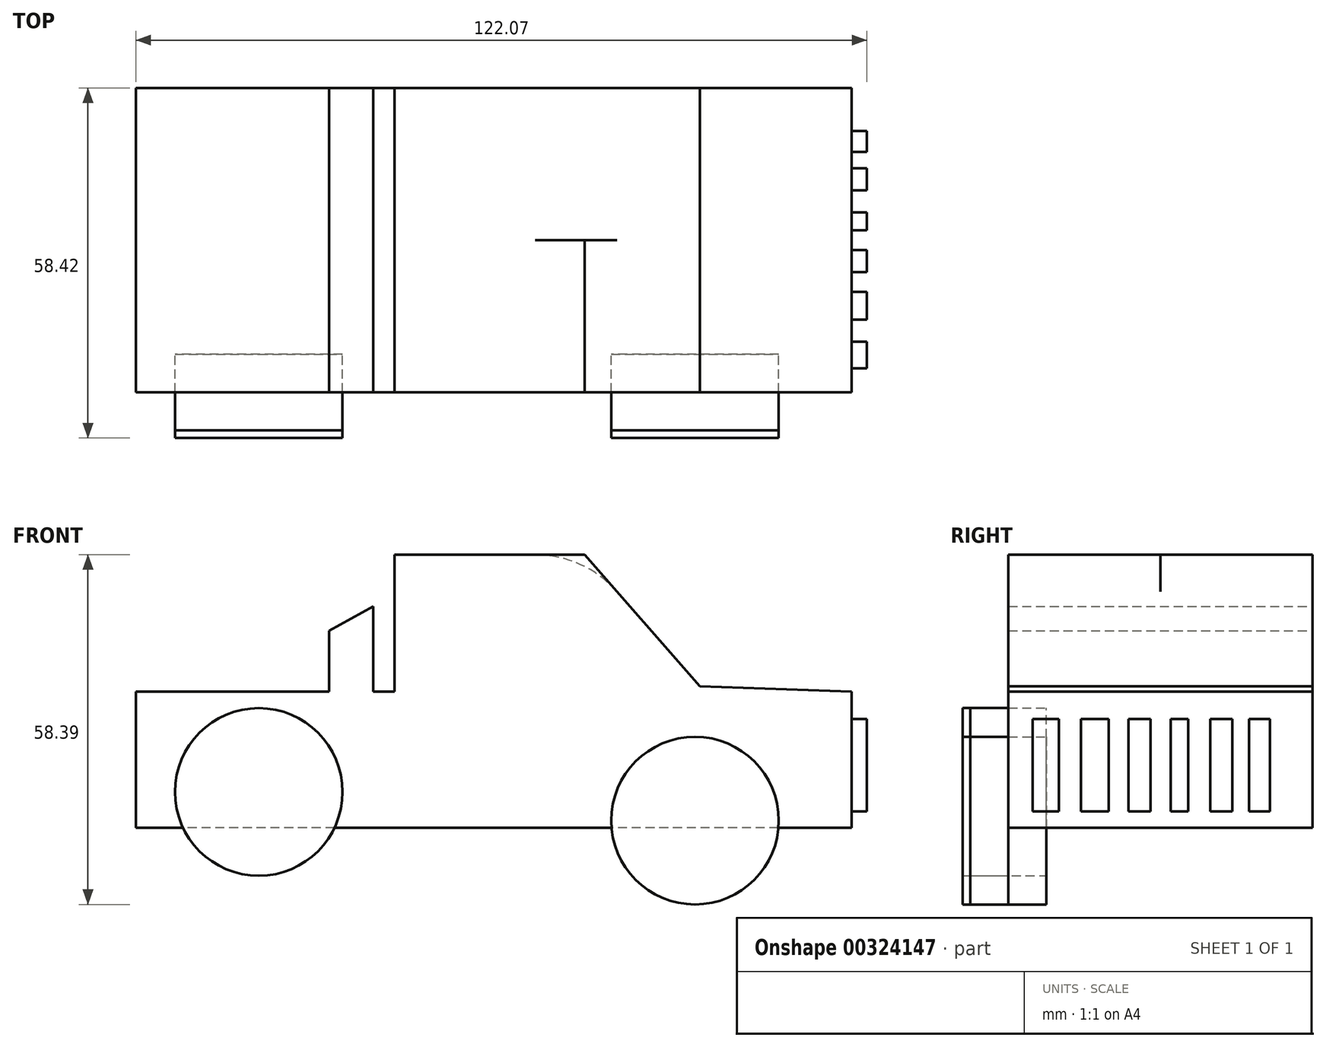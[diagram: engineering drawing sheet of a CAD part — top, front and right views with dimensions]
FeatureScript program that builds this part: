
annotation { "Feature Type Name" : "Feature", "Feature Type Description" : "" }
export const myFeature = defineFeature(function(context is Context, id is Id, definition is map)
    precondition{}
    {
        {
            var Q0;
            Q0=qCreatedBy(makeId("Front.planeOp"),FACE);
            var sketch = newSketch(context, id + "F0", { "sketchPlane" : qUnion([Q0])});
            skLineSegment(sketch, "E0", {"start": v(-43.82, 6.7) * mm, "end": v(-61.53, 6.7) * mm});
            skLineSegment(sketch, "E1", {"start": v(-61.53, 6.7) * mm, "end": v(-61.53, 29.43) * mm});
            skLineSegment(sketch, "E2", {"start": v(-61.53, 29.43) * mm, "end": v(-18.36, 29.43) * mm});
            skLineSegment(sketch, "E3", {"start": v(-18.36, 29.43) * mm, "end": v(-18.36, 52.3) * mm});
            skLineSegment(sketch, "E4", {"start": v(-18.36, 52.3) * mm, "end": v(13.39, 52.3) * mm});
            skLineSegment(sketch, "E5", {"start": v(13.39, 52.3) * mm, "end": v(32.61, 30.3) * mm});
            skLineSegment(sketch, "E6", {"start": v(32.61, 30.3) * mm, "end": v(58, 29.43) * mm});
            skLineSegment(sketch, "E7", {"start": v(22.23, 6.7) * mm, "end": v(-22.23, 6.7) * mm});
            skLineSegment(sketch, "E8", {"start": v(43.82, 6.7) * mm, "end": v(58, 6.7) * mm});
            skLineSegment(sketch, "E9", {"start": v(58, 29.43) * mm, "end": v(58, 6.7) * mm});
            skLineSegment(sketch, "E10", {"start": v(-29.3, 29.43) * mm, "end": v(-29.3, 39.59) * mm});
            skLineSegment(sketch, "E11", {"start": v(-29.3, 39.59) * mm, "end": v(-21.9, 43.65) * mm});
            skLineSegment(sketch, "E12", {"start": v(-21.9, 43.65) * mm, "end": v(-21.9, 29.43) * mm});
            skLineSegment(sketch, "E13", {"start": v(-61.53, 15.6) * mm, "end": v(-54.97, 15.6) * mm});
            skLineSegment(sketch, "E14", {"start": v(-54.97, 15.6) * mm, "end": v(-54.97, 6.7) * mm});
            skLineSegment(sketch, "E15", {"start": v(58, 21.75) * mm, "end": v(51.6, 21.75) * mm});
            skLineSegment(sketch, "E16", {"start": v(51.6, 21.75) * mm, "end": v(51.6, 29.43) * mm});
            skLineSegment(sketch, "E17", {"start": v(-54.97, 6.7) * mm, "end": v(58, 6.7) * mm});
            skSolve(sketch);
        }
        {
            var Q0;
            Q0 = qSketchRegion(id + "F0", true);
            extrude(context, id + "F1", {"entities" : qUnion([Q0]), "depth" : 50.8 * mm, "symmetric" : true});
        }
        {
            var Q0;
            Q0=makeQuery(id+"F1.opExtrude","CAP_FACE",FACE,{"disambiguationData":[OSD([sQuery(id+"F0.wireOp",EDGE,"jsAS9IXH-zQaz-s3Kv-pUAx-luXk4qnFeEN5"),sQuery(id+"F0.wireOp",EDGE,"7l7WPdtS-5suQ-AHQC-gmTl-FT6wHJ7VEzlQ"),sQuery(id+"F0.wireOp",EDGE,"E0"),sQuery(id+"F0.wireOp",EDGE,"E1"),sQuery(id+"F0.wireOp",EDGE,"E2"),sQuery(id+"F0.wireOp",EDGE,"E3"),sQuery(id+"F0.wireOp",EDGE,"E4"),sQuery(id+"F0.wireOp",EDGE,"E5"),sQuery(id+"F0.wireOp",EDGE,"E6"),sQuery(id+"F0.wireOp",EDGE,"E7"),sQuery(id+"F0.wireOp",EDGE,"qzmlPklc-gSGK-qsKq-jCsS-Svxx3mp7mvPV"),sQuery(id+"F0.wireOp",EDGE,"ulWVZydW-LgJQ-jYxT-eYgx-awK6DR7PkJde"),sQuery(id+"F0.wireOp",EDGE,"E8"),sQuery(id+"F0.wireOp",EDGE,"E9"),sQuery(id+"F0.wireOp",EDGE,"E10"),sQuery(id+"F0.wireOp",EDGE,"E11"),sQuery(id+"F0.wireOp",EDGE,"E12")])],"isStart":false});
            var sketch = newSketch(context, id + "F2", { "sketchPlane" : qUnion([Q0])});
            skLineSegment(sketch, "E18", {"start": v(-14.85, 49.04) * mm, "end": v(-14.85, 30.46) * mm});
            skLineSegment(sketch, "E19", {"start": v(-14.85, 30.46) * mm, "end": v(27.46, 30.46) * mm});
            skLineSegment(sketch, "E20", {"start": v(27.46, 30.46) * mm, "end": v(12.86, 49.04) * mm});
            skLineSegment(sketch, "E21", {"start": v(12.86, 49.04) * mm, "end": v(-14.85, 49.04) * mm});
            skSolve(sketch);
        }
        {
            var Q0;
            Q0=makeQuery(id+"F2.imprint","IMPRINT",FACE,{"disambiguationData":[TD([[makeQuery(id+"F2.imprint","IMPRINT",EDGE,{"derivedFrom":sQuery(id+"F2.wireOp",EDGE,"E18")}),1.0]])]});
            extrude(context, id + "F3", {"entities" : qUnion([Q0]), "operationType" : NewBodyOperationType.REMOVE, "oppositeDirection" : true, "depth" : 6.35 * mm});
        }
        {
            var Q0;
            Q0=makeQuery(id+"F1.opExtrude","SWEPT_EDGE",EDGE,{"disambiguationData":[OSD([sQuery(id+"F0.wireOp",EDGE,"E4"),sQuery(id+"F0.wireOp",EDGE,"E5")])]});
            fillet(context, id + "F4", {"entities" : qUnion([Q0]), "radius" : 18.1 * mm, "tangentPropagation" : true, "allowEdgeOverflow" : false});
        }
        {
            var Q0;
            Q0=makeQuery(id+"F1.opExtrude","SWEPT_FACE",FACE,{"disambiguationData":[OSD([sQuery(id+"F0.wireOp",EDGE,"E9")])]});
            var sketch = newSketch(context, id + "F5", { "sketchPlane" : qUnion([Q0])});
            skLineSegment(sketch, "E22.bottom", {"start": v(-21.39, 24.89) * mm, "end": v(21.75, 24.89) * mm});
            skLineSegment(sketch, "E22.top", {"start": v(-21.39, 9.4) * mm, "end": v(21.75, 9.4) * mm});
            skLineSegment(sketch, "E22.left", {"start": v(-21.39, 24.89) * mm, "end": v(-21.39, 9.4) * mm});
            skLineSegment(sketch, "E22.right", {"start": v(21.75, 24.89) * mm, "end": v(21.75, 9.4) * mm});
            skLineSegment(sketch, "E23", {"start": v(-16.96, 24.89) * mm, "end": v(-16.96, 9.4) * mm});
            skLineSegment(sketch, "E24", {"start": v(-13.27, 24.89) * mm, "end": v(-13.27, 9.4) * mm});
            skLineSegment(sketch, "E25", {"start": v(-8.66, 24.89) * mm, "end": v(-8.66, 9.4) * mm});
            skLineSegment(sketch, "E26", {"start": v(-5.35, 24.89) * mm, "end": v(-5.35, 9.4) * mm});
            skLineSegment(sketch, "E27", {"start": v(-1.66, 24.89) * mm, "end": v(-1.66, 9.4) * mm});
            skLineSegment(sketch, "E28", {"start": v(1.66, 24.89) * mm, "end": v(1.66, 9.4) * mm});
            skLineSegment(sketch, "E29", {"start": v(4.6, 24.89) * mm, "end": v(4.6, 9.4) * mm});
            skLineSegment(sketch, "E30", {"start": v(8.3, 24.89) * mm, "end": v(8.3, 9.4) * mm});
            skLineSegment(sketch, "E31", {"start": v(11.98, 24.89) * mm, "end": v(11.98, 9.4) * mm});
            skLineSegment(sketch, "E32", {"start": v(14.75, 24.89) * mm, "end": v(14.75, 9.4) * mm});
            skLineSegment(sketch, "E33", {"start": v(18.25, 24.89) * mm, "end": v(18.25, 9.4) * mm});
            skSolve(sketch);
        }
        {
            var Q0;
            {var subQ0=sQuery(id+"F5.wireOp",EDGE,"E22.left");Q0=makeQuery(id+"F5.imprint","IMPRINT",FACE,{"disambiguationData":[TD([[makeQuery(id+"F5.imprint","IMPRINT",EDGE,{"derivedFrom":subQ0}),1.0]])]});}
            var Q1;
            {var subQ0=sQuery(id+"F5.wireOp",EDGE,"E24");Q1=makeQuery(id+"F5.imprint","IMPRINT",FACE,{"disambiguationData":[TD([[makeQuery(id+"F5.imprint","IMPRINT",EDGE,{"derivedFrom":subQ0}),1.0]])]});}
            var Q2;
            {var subQ0=sQuery(id+"F5.wireOp",EDGE,"E26");Q2=makeQuery(id+"F5.imprint","IMPRINT",FACE,{"disambiguationData":[TD([[makeQuery(id+"F5.imprint","IMPRINT",EDGE,{"derivedFrom":subQ0}),1.0]])]});}
            var Q3;
            {var subQ0=sQuery(id+"F5.wireOp",EDGE,"E28");Q3=makeQuery(id+"F5.imprint","IMPRINT",FACE,{"disambiguationData":[TD([[makeQuery(id+"F5.imprint","IMPRINT",EDGE,{"derivedFrom":subQ0}),1.0]])]});}
            var Q4;
            {var subQ0=sQuery(id+"F5.wireOp",EDGE,"E30");Q4=makeQuery(id+"F5.imprint","IMPRINT",FACE,{"disambiguationData":[TD([[makeQuery(id+"F5.imprint","IMPRINT",EDGE,{"derivedFrom":subQ0}),1.0]])]});}
            var Q5;
            {var subQ0=sQuery(id+"F5.wireOp",EDGE,"E32");Q5=makeQuery(id+"F5.imprint","IMPRINT",FACE,{"disambiguationData":[TD([[makeQuery(id+"F5.imprint","IMPRINT",EDGE,{"derivedFrom":subQ0}),1.0]])]});}
            extrude(context, id + "F6", {"entities" : qUnion([Q0, Q1, Q2, Q3, Q4, Q5]), "operationType" : NewBodyOperationType.ADD, "depth" : 2.54 * mm});
        }
        {
            var Q0;
            Q0 = qSketchRegion(id + "F0", true);
            extrude(context, id + "F7", {"entities" : qUnion([Q0]), "operationType" : NewBodyOperationType.ADD, "depth" : 25.4 * mm});
        }
        {
            var Q0;
            {var subQ0=sQuery(id+"F0.wireOp",EDGE,"E17");var subQ1=sQuery(id+"F0.wireOp",EDGE,"E12");var subQ2=sQuery(id+"F0.wireOp",EDGE,"E11");var subQ3=sQuery(id+"F0.wireOp",EDGE,"E10");var subQ4=sQuery(id+"F0.wireOp",EDGE,"E9");var subQ5=sQuery(id+"F0.wireOp",EDGE,"E6");var subQ6=sQuery(id+"F0.wireOp",EDGE,"E5");var subQ7=sQuery(id+"F0.wireOp",EDGE,"E4");var subQ8=sQuery(id+"F0.wireOp",EDGE,"E3");var subQ9=sQuery(id+"F0.wireOp",EDGE,"E2");var subQ10=sQuery(id+"F0.wireOp",EDGE,"E1");var subQ11=sQuery(id+"F0.wireOp",EDGE,"E0");Q0=makeQuery(id+"F7.boolean.opBoolean","MERGE",FACE,{"derivedFrom":[makeQuery(id+"F1.opExtrude","CAP_FACE",FACE,{"disambiguationData":[OSD([subQ11,subQ10,subQ9,subQ8,subQ7,subQ6,subQ5,subQ4,subQ3,subQ2,subQ1,subQ0])],"isStart":false}),makeQuery(id+"F7.opExtrude","CAP_FACE",FACE,{"disambiguationData":[OSD([subQ11,subQ10,subQ9,subQ8,subQ7,subQ6,subQ5,subQ4,subQ3,subQ2,subQ1,subQ0])],"isStart":false})]});}
            var sketch = newSketch(context, id + "F8", { "sketchPlane" : qUnion([Q0])});
            skArc(sketch, "E34", {"start": v(-53.66, 6.7) * mm, "mid": v(-41.02, -1.3) * mm, "end": v(-28.38, 6.7) * mm});
            skArc(sketch, "E35", {"start": v(17.88, 6.7) * mm, "mid": v(31.82, -6.1) * mm, "end": v(45.76, 6.7) * mm});
            skArc(sketch, "E36", {"start": v(-28.38, 6.7) * mm, "mid": v(-41.02, 26.67) * mm, "end": v(-53.66, 6.7) * mm});
            skArc(sketch, "E37", {"start": v(45.76, 6.7) * mm, "mid": v(31.82, 21.88) * mm, "end": v(17.88, 6.7) * mm});
            skSolve(sketch);
        }
        {
            var Q0;
            {var subQ0=sQuery(id+"F8.wireOp",EDGE,"E34");Q0=makeQuery(id+"F8.imprint","IMPRINT",FACE,{"disambiguationData":[TD([[makeQuery(id+"F8.imprint","IMPRINT",EDGE,{"derivedFrom":subQ0}),1.0]])]});}
            var Q1;
            {var subQ0=sQuery(id+"F8.wireOp",EDGE,"E36");Q1=makeQuery(id+"F8.imprint","IMPRINT",FACE,{"disambiguationData":[TD([[makeQuery(id+"F8.imprint","IMPRINT",EDGE,{"derivedFrom":subQ0}),1.0]])]});}
            var Q2;
            {var subQ0=sQuery(id+"F8.wireOp",EDGE,"E37");Q2=makeQuery(id+"F8.imprint","IMPRINT",FACE,{"disambiguationData":[TD([[makeQuery(id+"F8.imprint","IMPRINT",EDGE,{"derivedFrom":subQ0}),1.0]])]});}
            var Q3;
            {var subQ0=sQuery(id+"F8.wireOp",EDGE,"E34");Q3=makeQuery(id+"F8.imprint","IMPRINT",FACE,{"disambiguationData":[TD([[makeQuery(id+"F8.imprint","IMPRINT",EDGE,{"derivedFrom":subQ0}),1.0]])]});}
            var Q4;
            {var subQ0=sQuery(id+"F8.wireOp",EDGE,"E35");Q4=makeQuery(id+"F8.imprint","IMPRINT",FACE,{"disambiguationData":[TD([[makeQuery(id+"F8.imprint","IMPRINT",EDGE,{"derivedFrom":subQ0}),1.0]])]});}
            var Q5;
            {var subQ0=sQuery(id+"F8.wireOp",EDGE,"E36");Q5=makeQuery(id+"F8.imprint","IMPRINT",FACE,{"disambiguationData":[TD([[makeQuery(id+"F8.imprint","IMPRINT",EDGE,{"derivedFrom":subQ0}),1.0]])]});}
            var Q6;
            {var subQ0=sQuery(id+"F8.wireOp",EDGE,"E37");Q6=makeQuery(id+"F8.imprint","IMPRINT",FACE,{"disambiguationData":[TD([[makeQuery(id+"F8.imprint","IMPRINT",EDGE,{"derivedFrom":subQ0}),1.0]])]});}
            var Q7;
            {var subQ0=sQuery(id+"F8.wireOp",EDGE,"E34");Q7=makeQuery(id+"F8.imprint","IMPRINT",FACE,{"disambiguationData":[TD([[makeQuery(id+"F8.imprint","IMPRINT",EDGE,{"derivedFrom":subQ0}),1.0]])]});}
            extrude(context, id + "F9", {"entities" : qUnion([Q0, Q1, Q2, Q3, Q4, Q5, Q6, Q7]), "depth" : 12.7 * mm, "symmetric" : true});
        }
        {
            var Q0;
            Q0 = qSketchRegion(id + "F8", true);
            extrude(context, id + "F10", {"entities" : qUnion([Q0]), "depth" : 7.62 * mm});
        }
    });
